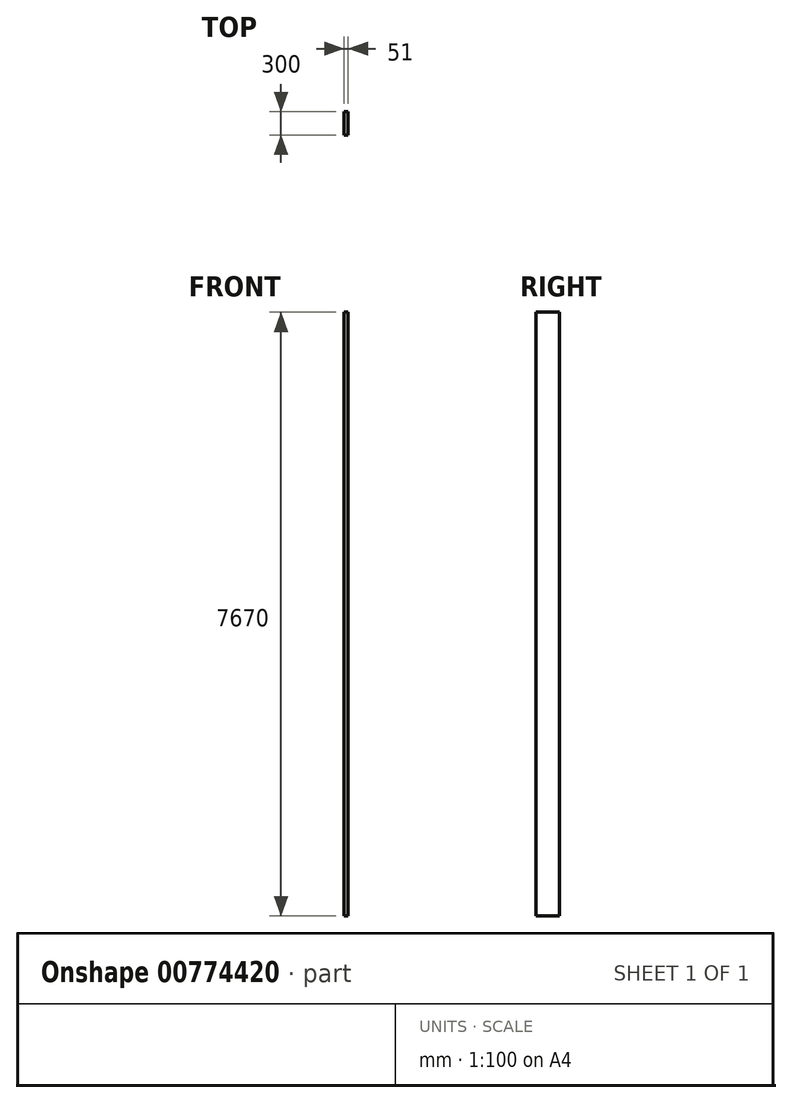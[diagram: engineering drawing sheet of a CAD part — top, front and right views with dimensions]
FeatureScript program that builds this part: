
annotation { "Feature Type Name" : "Feature", "Feature Type Description" : "" }
export const myFeature = defineFeature(function(context is Context, id is Id, definition is map)
    precondition{}
    {
        {
            var Q0;
            Q0=qCreatedBy(makeId("Top.planeOp"),FACE);
            var sketch = newSketch(context, id + "F0", { "sketchPlane" : qUnion([Q0])});
            skLineSegment(sketch, "E0.bottom", {"start": v(0, 0) * mm, "end": v(51, 0) * mm});
            skLineSegment(sketch, "E0.top", {"start": v(0, 300) * mm, "end": v(51, 300) * mm});
            skLineSegment(sketch, "E0.left", {"start": v(0, 0) * mm, "end": v(0, 300) * mm});
            skLineSegment(sketch, "E0.right", {"start": v(51, 0) * mm, "end": v(51, 300) * mm});
            skSolve(sketch);
        }
        {
            var Q0;
            Q0=qSketchRegion(id+"F0",true);
            extrude(context, id + "F1", {"entities" : qUnion([Q0]), "depth" : 7670 * mm, "offsetDistance" : 25 * mm});
        }
    });
